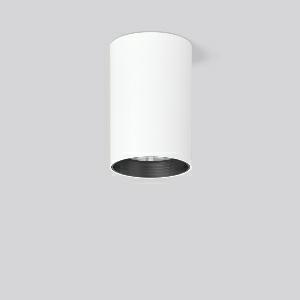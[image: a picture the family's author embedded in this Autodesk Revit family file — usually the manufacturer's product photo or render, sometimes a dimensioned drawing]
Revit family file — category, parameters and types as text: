
# Revit family: heledon_maxi_a_931220_002_3_76_68b2
name_source: partatom
category: Lighting Fixtures
units: mm (PartAtom-declared; Revit-internal decimal feet)

## family parameters
Cut with Voids When Loaded = No
Host = Face
Light Source = No
Part Type = Normal
Room Calculation Point = No
Round Connector Dimension = Use Diameter
Shared = No

## types (1)
- HELEDON maxi A (1 x LED Modul 935, 2900 lm, 3500)
    Apparent Load = 25 VA
    Approval mark = CE
    CIE Flux Codes = 97 100 100 100 100
    Color Rendering = 92
    Color Temperature = 3500
    Default Elevation = 1800 mm
    Description = Series: HELEDON maxi
Cylindrical surface-mounted downlight. Housing: die-cast aluminium, powder-coated. Internal ceiling frame polycarbonate with bayonet mounting. Black plastic ring and recessed LED to prevent glare from the side. Optical assembly with lens made of plastic (polycarbonate) for the best homogeneous light distribution - can be changed without tools. Best colour rendering index Ra>90. Suitable for Ceiling mounting. Easy installation with a separate ceiling frame with bayonet mounting and plug connection. Driver integrated. Connected via plug-in connector. High quality converter without flickering and stroboscopic effect. The following accessories can be mounted without use of tools: interchangeable lenses, decorative glasses, honeycomb louvre, clear and frosted diffusers, white interchangeable plastic ring. 
Colour: traffic white, matt (RAL 9016)
Diameter: 123 mm
Height: 183 mm
Lamp: LED
Socket: without socket
Colour temperature: 3500K
Colour rendering index (CRI): 92
System power: 25 W
Rated luminous flux: 2900 lm
Luminous efficiency: 116 lm/W
Control gear: Converter, dimmable, DALI
Protection class: I
Type of protection: IP 20
    Height = 183 mm
    Lamp = 1 x LED Modul 935
    Lamp Light Flux = 2900 lm
    Lamp count = 1
    Length = 123 mm
    Lifetime = 50000 h
    Luminous efficacy = 116 lm/W
    Manufacturer = RZB
    ModVariant = No
    Model = 931220.002.3.76
    Mounting Place = Ceiling
    Mounting Type = Surface mounted
    Number of Poles = 1
    OnlyDefault = Yes
    Power Factor = 1
    Product Name = HELEDON maxi A
    Product group = Surface mounted downlights
    ProductGroupID = 302
    Protection Class = Protection class I
    Protection Degree = IP 20
    RLX_Detail_Level = 1
    RLX_Emergency_Light_Flux = 0 lm
    RLX_Emergency_Type = 0
    RLX_Emergency_Type_DB = No
    RlxData = <blob elided: 96045 chars, md5=23aa77e9>
    Socket = socket
    Standby Power = 0 W
    System Light Flux = 2900 lm
    System Power = 25 W
    Type Comments = Product without accessories
    Type Image = 931193.002.jpg
    URL = http://relux.com
    VarID = ---
    Voltage = 230 V
    Voltage Range = 220-240 V
    Weight = 0.00 kg
    Width = 0 mm  [stored 0 ft]

note: [stored X ft] marks values corroborated as IEEE doubles in the binary element streams (Revit-internal decimal feet)

## geometry (parser evidence)
native form markers: Blend x4, Sweep x10
no freeform markers — native parametric forms only
